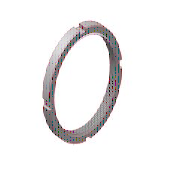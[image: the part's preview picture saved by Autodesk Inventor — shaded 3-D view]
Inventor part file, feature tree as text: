
AUTODESK INVENTOR PART (.ipt)
format: ipt  version: 2021 (Build 250183000, 183)  size: 206,848 bytes
history: native  units: mm (DEFAULTED — no unit token found)
features: sketch x3, hole x1, extrude x1, pattern_circular x1, other x1, plane x1
ambient origin geometry x8: Origin, YZ Plane, XZ Plane, XY Plane, X Axis, Y Axis, Z Axis, Center Point
bodies: Solid1 (feature_tree), Body (feature_tree)
feature tree (8):
  hole  "Thread"  [1 undecoded]
  extrude  "Groove1"  Depth=2.6mm
  pattern_circular  "Grooves1"  Angle=30.0deg  [1 undecoded]
  other  "Work Axis1"
  plane  "Work Plane1"
  sketch  "Sketch1"  dims[d0=90.0deg d1=210.0mm]
  sketch  "Sketch2"  dims[d2=26.0mm]
  sketch  "Sketch3"  dims[d3=161.752404mm d4=6.0mm d5=4.0mm d6=2.0mm d7=14.3117mm d8=8.0mm d9=0.0mm d10=8.5mm d11=30.0deg d12=8.0mm d13=8.0mm d14=98.0mm d23=10.0mm d15=0.0mm d16=40.0mm d17=360.0deg d18=2.6mm d19=4.125mm d20=45.0deg d21=4.125mm d22=45.0deg d25=0.0mm d40=8.5mm d41=4.125mm d42=4.125mm d45=90.0deg d47=0.0mm d48=0.0mm]
note: 2 required parameter values undecoded (feature->parameter linkage not recoverable at this tier; creation-order binding heuristic only, values carry confidence <= 0.55)
